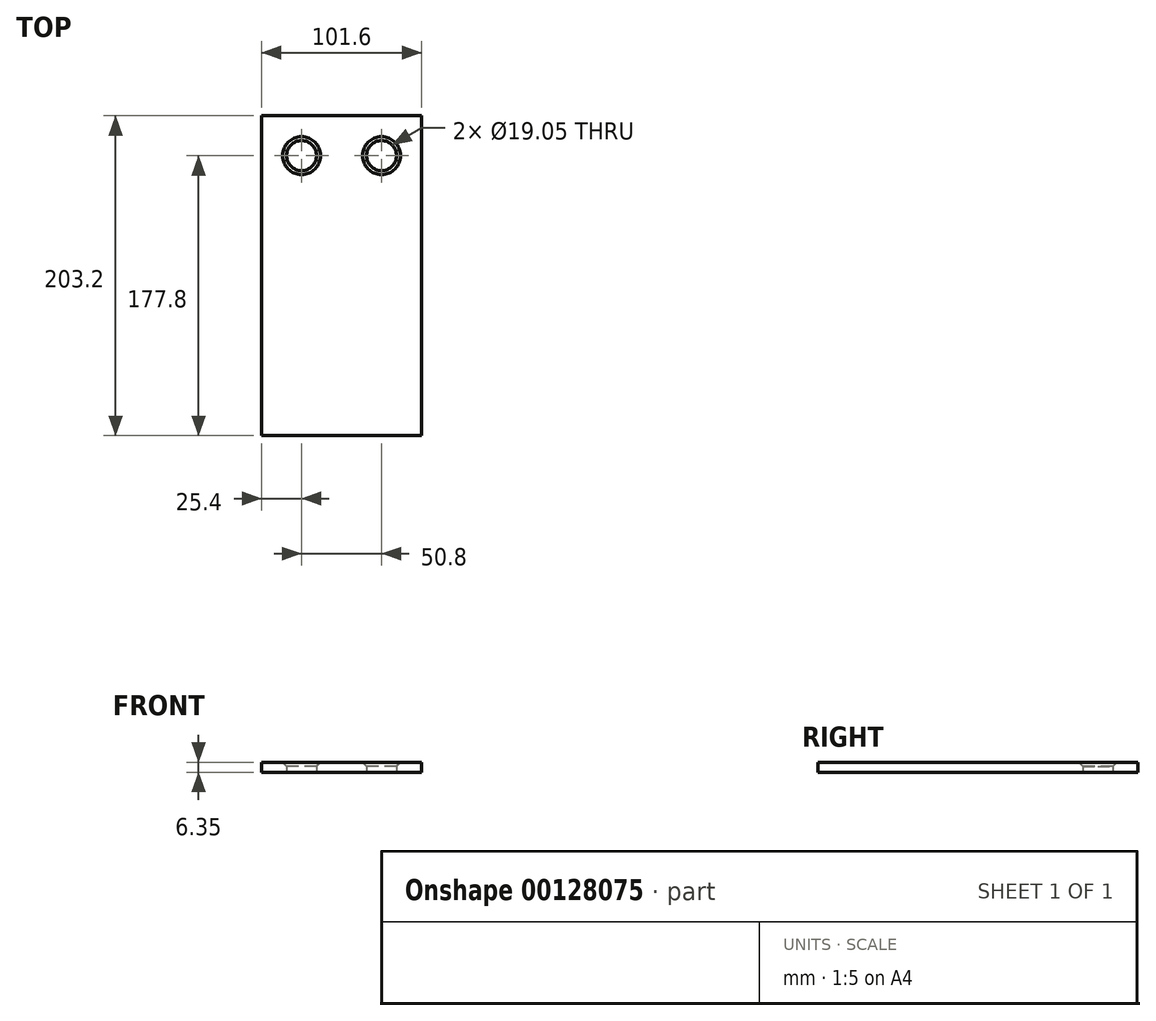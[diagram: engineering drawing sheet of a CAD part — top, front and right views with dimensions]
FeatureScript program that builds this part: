
annotation { "Feature Type Name" : "Feature", "Feature Type Description" : "" }
export const myFeature = defineFeature(function(context is Context, id is Id, definition is map)
    precondition{}
    {
        {
            var Q0;
            Q0=qCreatedBy(makeId("Top.planeOp"),FACE);
            var sketch = newSketch(context, id + "F0", { "sketchPlane" : qUnion([Q0])});
            skLineSegment(sketch, "E0", {"start": v(-50.8, 101.6) * mm, "end": v(-50.8, 0) * mm});
            skLineSegment(sketch, "E1", {"start": v(-50.8, 101.6) * mm, "end": v(50.8, 101.6) * mm});
            skLineSegment(sketch, "E2", {"start": v(50.8, 101.6) * mm, "end": v(50.8, 0) * mm});
            skLineSegment(sketch, "E3.MirrorCS", {"start": v(-50.8, -101.6) * mm, "end": v(-50.8, 0) * mm});
            skLineSegment(sketch, "E4.MirrorCS", {"start": v(-50.8, -101.6) * mm, "end": v(50.8, -101.6) * mm});
            skLineSegment(sketch, "E5.MirrorCS", {"start": v(50.8, -101.6) * mm, "end": v(50.8, 0) * mm});
            skCircle(sketch, "E6", {"center": v(-25.4, 76.2) * mm, "radius": 9.53 * mm});
            skCircle(sketch, "E7", {"center": v(25.4, 76.2) * mm, "radius": 9.53 * mm});
            skSolve(sketch);
        }
        {
            var Q0;
            Q0 = qSketchRegion(id + "F0", true);
            extrude(context, id + "F1", {"entities" : qUnion([Q0]), "depth" : 6.35 * mm});
        }
        {
            var Q0;
            Q0=makeQuery(id+"F1.opExtrude","CAP_EDGE",EDGE,{"disambiguationData":[OSD([sQuery(id+"F0.wireOp",EDGE,"E6")])],"isStart":false});
            var Q1;
            Q1=makeQuery(id+"F1.opExtrude","CAP_EDGE",EDGE,{"disambiguationData":[OSD([sQuery(id+"F0.wireOp",EDGE,"E7")])],"isStart":false});
            chamfer(context, id + "F2", {"entities" : qUnion([Q0, Q1]), "width" : 2.54 * mm, "tangentPropagation" : true});
        }
    });
